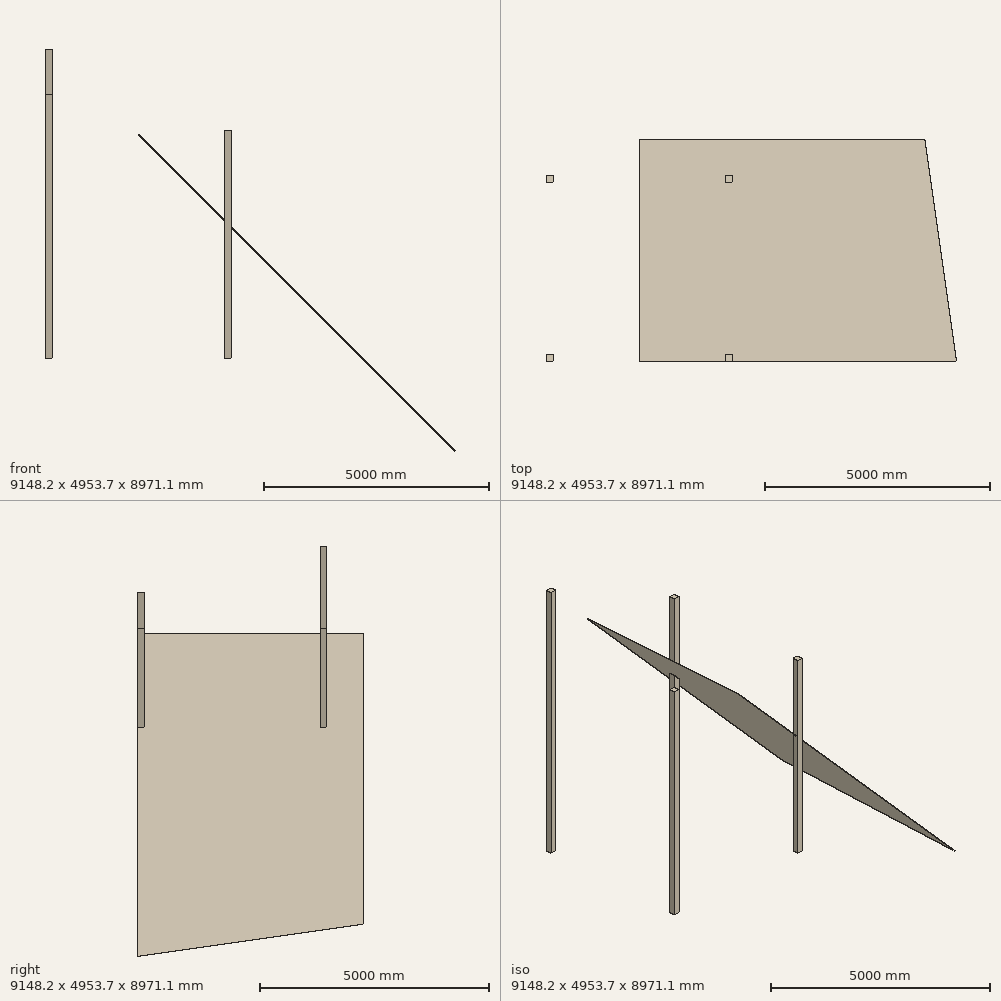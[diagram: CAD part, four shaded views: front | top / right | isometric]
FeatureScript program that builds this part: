
annotation { "Feature Type Name" : "Feature", "Feature Type Description" : "" }
export const myFeature = defineFeature(function(context is Context, id is Id, definition is map)
    precondition{}
    {
        {
            var Q0;
            Q0=qCreatedBy(makeId("Front.planeOp"),FACE);
            var sketch = newSketch(context, id + "F0", { "sketchPlane" : qUnion([Q0])});
            skLineSegment(sketch, "E0", {"start": v(3000, 7000) * mm, "end": v(3000, 6000) * mm, "construction": true});
            skLineSegment(sketch, "E1", {"start": v(3000, 6000) * mm, "end": v(3000, 3000) * mm, "construction": true});
            skLineSegment(sketch, "E2", {"start": v(3000, 3000) * mm, "end": v(0, 3000) * mm, "construction": true});
            skLineSegment(sketch, "E3", {"start": v(0, 3000) * mm, "end": v(0, 10000) * mm, "construction": true});
            skLineSegment(sketch, "E4", {"start": v(3000, 6000) * mm, "end": v(0, 6000) * mm, "construction": true});
            skLineSegment(sketch, "E5", {"start": v(0, 3000) * mm, "end": v(0, 0) * mm, "construction": true});
            skLineSegment(sketch, "E6", {"start": v(0, 0) * mm, "end": v(7000, 0) * mm, "construction": true});
            skLineSegment(sketch, "E7", {"start": v(3000, 6000) * mm, "end": v(11000, 3000) * mm, "construction": true});
            skLineSegment(sketch, "E8", {"start": v(5828, 3000) * mm, "end": v(11000, 3000) * mm, "construction": true});
            skLineSegment(sketch, "E9", {"start": v(7000, 3000) * mm, "end": v(7000, 4500) * mm, "construction": true});
            skLineSegment(sketch, "E10", {"start": v(3000, 3000) * mm, "end": v(4000, 3000) * mm, "construction": true});
            skLineSegment(sketch, "E11", {"start": v(4000, 3000) * mm, "end": v(4000, 5625) * mm, "construction": true});
            skLineSegment(sketch, "E12.0", {"start": v(3000, 7000) * mm, "end": v(0, 7000) * mm, "construction": true});
            skLineSegment(sketch, "E13", {"start": v(0, 6500) * mm, "end": v(3500, 6500) * mm, "construction": true});
            skLineSegment(sketch, "E14", {"start": v(3500, 6500) * mm, "end": v(0, 10000) * mm, "construction": true});
            skFitSpline(sketch, "E15", {"points": [v(3000, 6000) * mm, v(7000, 5200) * mm, v(9500, 3000) * mm], "startDerivative": vector(10495.04, -690.46) * mm, "endDerivative": vector(2972.96, -5651.08) * mm, "construction": true});
            skArc(sketch, "E16", {"start": v(9099.2, 3361.06) * mm, "mid": v(6978.83, 5128.79) * mm, "end": v(4291.38, 5760) * mm, "construction": true});
            skLineSegment(sketch, "E17", {"start": v(3075, 2870) * mm, "end": v(3130.8, 2870) * mm});
            skLineSegment(sketch, "E18", {"start": v(3130.8, 2870) * mm, "end": v(3181.6, 2920.8) * mm});
            skLineSegment(sketch, "E19", {"start": v(3181.6, 2920.8) * mm, "end": v(3282.6, 2920.8) * mm});
            skLineSegment(sketch, "E20", {"start": v(3282.6, 2920.8) * mm, "end": v(3333.4, 2870) * mm});
            skLineSegment(sketch, "E21", {"start": v(3232.1, 2920.8) * mm, "end": v(3232.1, 2870) * mm, "construction": true});
            skLineSegment(sketch, "E22.0", {"start": v(3075, 2990) * mm, "end": v(4015, 2990) * mm});
            skLineSegment(sketch, "E23", {"start": v(3333.4, 2870) * mm, "end": v(3389.2, 2870) * mm});
            skLineSegment(sketch, "E24.1.0.0", {"start": v(3389, 2870) * mm, "end": v(3444.8, 2870) * mm});
            skLineSegment(sketch, "E24.1.0.1", {"start": v(3444.8, 2870) * mm, "end": v(3495.6, 2920.8) * mm});
            skLineSegment(sketch, "E24.1.0.2", {"start": v(3495.6, 2920.8) * mm, "end": v(3596.6, 2920.8) * mm});
            skLineSegment(sketch, "E24.1.0.3", {"start": v(3596.6, 2920.8) * mm, "end": v(3647.4, 2870) * mm});
            skLineSegment(sketch, "E24.1.0.4", {"start": v(3647.4, 2870) * mm, "end": v(3703.2, 2870) * mm});
            skLineSegment(sketch, "E24.2.0.0", {"start": v(3703, 2870) * mm, "end": v(3758.8, 2870) * mm});
            skLineSegment(sketch, "E24.2.0.1", {"start": v(3758.8, 2870) * mm, "end": v(3809.6, 2920.8) * mm});
            skLineSegment(sketch, "E24.2.0.2", {"start": v(3809.6, 2920.8) * mm, "end": v(3910.6, 2920.8) * mm});
            skLineSegment(sketch, "E24.2.0.3", {"start": v(3910.6, 2920.8) * mm, "end": v(3961.4, 2870) * mm});
            skLineSegment(sketch, "E24.2.0.4", {"start": v(3961.4, 2870) * mm, "end": v(4017.2, 2870) * mm});
            skLineSegment(sketch, "E24.direction1", {"start": v(3075, 2870) * mm, "end": v(3389, 2870) * mm, "construction": true});
            skLineSegment(sketch, "E25", {"start": v(3075, 2990) * mm, "end": v(3075, 2870) * mm});
            skLineSegment(sketch, "E26", {"start": v(4015, 2990) * mm, "end": v(4015, 2870) * mm});
            skLineSegment(sketch, "E27.0", {"start": v(3075, 3000) * mm, "end": v(4015, 3000) * mm});
            skLineSegment(sketch, "E28.0", {"start": v(3075, 6029.43) * mm, "end": v(3075, 3000) * mm, "construction": true});
            skLineSegment(sketch, "E29", {"start": v(3000, 2990) * mm, "end": v(3000, 2720) * mm});
            skLineSegment(sketch, "E30", {"start": v(3000, 2990) * mm, "end": v(3095, 2990) * mm});
            skLineSegment(sketch, "E31", {"start": v(3095, 2990) * mm, "end": v(3095, 2979.5) * mm});
            skLineSegment(sketch, "E32", {"start": v(3095, 2979.5) * mm, "end": v(3018, 2979.5) * mm});
            skLineSegment(sketch, "E33", {"start": v(3006, 2967.5) * mm, "end": v(3006, 2742.5) * mm});
            skLineSegment(sketch, "E34", {"start": v(3018, 2730.5) * mm, "end": v(3095, 2730.5) * mm});
            skLineSegment(sketch, "E35", {"start": v(3095, 2730.5) * mm, "end": v(3095, 2720) * mm});
            skLineSegment(sketch, "E36", {"start": v(3095, 2720) * mm, "end": v(3000, 2720) * mm});
            skPoint(sketch, "E37.visualSharp", {"position": v(3006, 2979.5) * mm});
            skArc(sketch, "E37.filletArc", {"start": v(3018, 2979.5) * mm, "mid": v(3009.51, 2975.99) * mm, "end": v(3006, 2967.5) * mm});
            skPoint(sketch, "E38.visualSharp", {"position": v(3006, 2730.5) * mm});
            skArc(sketch, "E38.filletArc", {"start": v(3006, 2742.5) * mm, "mid": v(3009.51, 2734.01) * mm, "end": v(3018, 2730.5) * mm});
            skLineSegment(sketch, "E39", {"start": v(3095, 2730.5) * mm, "end": v(3095, 2870.5) * mm});
            skLineSegment(sketch, "E40", {"start": v(3095, 2730.5) * mm, "end": v(3037, 2730.5) * mm});
            skLineSegment(sketch, "E41", {"start": v(3037, 2730.5) * mm, "end": v(3037, 2738.6) * mm});
            skLineSegment(sketch, "E42", {"start": v(3037, 2738.6) * mm, "end": v(3078.9, 2738.6) * mm});
            skLineSegment(sketch, "E43", {"start": v(3090.9, 2750.6) * mm, "end": v(3090.9, 2850.4) * mm});
            skLineSegment(sketch, "E44", {"start": v(3078.9, 2862.4) * mm, "end": v(3037, 2862.4) * mm});
            skLineSegment(sketch, "E45", {"start": v(3037, 2862.4) * mm, "end": v(3037, 2870.5) * mm});
            skLineSegment(sketch, "E46", {"start": v(3037, 2870.5) * mm, "end": v(3095, 2870.5) * mm});
            skPoint(sketch, "E47.visualSharp", {"position": v(3090.9, 2738.6) * mm});
            skArc(sketch, "E47.filletArc", {"start": v(3078.9, 2738.6) * mm, "mid": v(3087.39, 2742.11) * mm, "end": v(3090.9, 2750.6) * mm});
            skPoint(sketch, "E48.visualSharp", {"position": v(3090.9, 2862.4) * mm});
            skArc(sketch, "E48.filletArc", {"start": v(3090.9, 2850.4) * mm, "mid": v(3087.39, 2858.89) * mm, "end": v(3078.9, 2862.4) * mm});
            skLineSegment(sketch, "E49", {"start": v(0, 10000) * mm, "end": v(-3500, 6500) * mm, "construction": true});
            skFitSpline(sketch, "E50.MirrorCS", {"points": [v(-3000, 6000) * mm, v(-7000, 5200) * mm, v(-9500, 3000) * mm], "startDerivative": vector(-10495.04, -690.46) * mm, "endDerivative": vector(-2972.96, -5651.08) * mm, "construction": true});
            skLineSegment(sketch, "E51", {"start": v(0, 3000) * mm, "end": v(-9500, 3000) * mm, "construction": true});
            skLineSegment(sketch, "E52", {"start": v(0, 0) * mm, "end": v(-7000, 0) * mm, "construction": true});
            skLineSegment(sketch, "E53", {"start": v(7000, 0) * mm, "end": v(7000, 3000) * mm, "construction": true});
            skLineSegment(sketch, "E54", {"start": v(3000, 0) * mm, "end": v(3000, 3000) * mm, "construction": true});
            skLineSegment(sketch, "E55.MirrorCS", {"start": v(-7000, 0) * mm, "end": v(-7000, 3000) * mm, "construction": true});
            skLineSegment(sketch, "E56.MirrorCS", {"start": v(-3000, 0) * mm, "end": v(-3000, 3000) * mm, "construction": true});
            skLineSegment(sketch, "E57.0", {"start": v(8000, -1400) * mm, "end": v(8000, 0) * mm, "construction": true});
            skLineSegment(sketch, "E58.0", {"start": v(-8000, -1400) * mm, "end": v(8000, -1400) * mm, "construction": true});
            skLineSegment(sketch, "E59", {"start": v(-8000, 0) * mm, "end": v(-8000, -1400) * mm, "construction": true});
            skSolve(sketch);
        }
        {
            var Q0;
            Q0=qCreatedBy(makeId("Top.planeOp"),FACE);
            var sketch = newSketch(context, id + "F1", { "sketchPlane" : qUnion([Q0])});
            skLineSegment(sketch, "E60.bottom", {"start": v(7000, -7000) * mm, "end": v(-7000, -7000) * mm, "construction": true});
            skLineSegment(sketch, "E60.top", {"start": v(7000, 7000) * mm, "end": v(-7000, 7000) * mm, "construction": true});
            skLineSegment(sketch, "E60.left", {"start": v(7000, -7000) * mm, "end": v(7000, 7000) * mm, "construction": true});
            skLineSegment(sketch, "E60.right", {"start": v(-7000, -7000) * mm, "end": v(-7000, 7000) * mm, "construction": true});
            skLineSegment(sketch, "E61", {"start": v(0, 0) * mm, "end": v(0, -7000) * mm, "construction": true});
            skLineSegment(sketch, "E62.bottom", {"start": v(-3000, 3000) * mm, "end": v(3000, 3000) * mm, "construction": true});
            skLineSegment(sketch, "E62.top", {"start": v(-3000, -3000) * mm, "end": v(3000, -3000) * mm, "construction": true});
            skLineSegment(sketch, "E62.left", {"start": v(-3000, 3000) * mm, "end": v(-3000, -3000) * mm, "construction": true});
            skLineSegment(sketch, "E62.right", {"start": v(3000, 3000) * mm, "end": v(3000, -3000) * mm, "construction": true});
            skLineSegment(sketch, "E63", {"start": v(0, 0) * mm, "end": v(7000, 0) * mm, "construction": true});
            skLineSegment(sketch, "E64.bottom", {"start": v(2925, -2925) * mm, "end": v(3075, -2925) * mm});
            skLineSegment(sketch, "E64.top", {"start": v(2925, -3075) * mm, "end": v(3075, -3075) * mm});
            skLineSegment(sketch, "E64.left", {"start": v(2925, -2925) * mm, "end": v(2925, -3075) * mm});
            skLineSegment(sketch, "E64.right", {"start": v(3075, -2925) * mm, "end": v(3075, -3075) * mm});
            skLineSegment(sketch, "E65.bottom", {"start": v(6925, -7075) * mm, "end": v(7075, -7075) * mm});
            skLineSegment(sketch, "E65.top", {"start": v(6925, -6925) * mm, "end": v(7075, -6925) * mm});
            skLineSegment(sketch, "E65.left", {"start": v(6925, -6925) * mm, "end": v(6925, -7075) * mm});
            skLineSegment(sketch, "E65.right", {"start": v(7075, -6925) * mm, "end": v(7075, -7075) * mm});
            skLineSegment(sketch, "E66.bottom", {"start": v(7075, -2925) * mm, "end": v(6925, -2925) * mm});
            skLineSegment(sketch, "E66.top", {"start": v(7075, -3075) * mm, "end": v(6925, -3075) * mm});
            skLineSegment(sketch, "E66.left", {"start": v(7075, -2925) * mm, "end": v(7075, -3075) * mm});
            skLineSegment(sketch, "E66.right", {"start": v(6925, -2925) * mm, "end": v(6925, -3075) * mm});
            skLineSegment(sketch, "E67.bottom", {"start": v(3075, -6925) * mm, "end": v(2925, -6925) * mm});
            skLineSegment(sketch, "E67.top", {"start": v(3075, -7075) * mm, "end": v(2925, -7075) * mm});
            skLineSegment(sketch, "E67.left", {"start": v(3075, -6925) * mm, "end": v(3075, -7075) * mm});
            skLineSegment(sketch, "E67.right", {"start": v(2925, -6925) * mm, "end": v(2925, -7075) * mm});
            skLineSegment(sketch, "E68.bottom", {"start": v(-5000, 15306.58) * mm, "end": v(5000, 15306.58) * mm, "construction": true});
            skLineSegment(sketch, "E68.top", {"start": v(-5000, 12106.58) * mm, "end": v(5000, 12106.58) * mm, "construction": true});
            skLineSegment(sketch, "E68.left", {"start": v(-5000, 15306.58) * mm, "end": v(-5000, 12106.58) * mm, "construction": true});
            skLineSegment(sketch, "E68.right", {"start": v(5000, 15306.58) * mm, "end": v(5000, 12106.58) * mm, "construction": true});
            skLineSegment(sketch, "E69.0", {"start": v(-5000, 10906.58) * mm, "end": v(5000, 10906.58) * mm, "construction": true});
            skPoint(sketch, "E70", {"position": v(0, 10906.58) * mm});
            skSolve(sketch);
        }
        {
            var Q0;
            Q0=qCreatedBy(makeId("Top.planeOp"),FACE);
            cPlane(context, id + "F2", {"entities" : qUnion([Q0]), "cplaneType" : CPlaneType.OFFSET, "offset" : 3000 * mm, "width" : 150 * mm, "height" : 150 * mm});
        }
        {
            var Q0;
            Q0=qCreatedBy(id+"F2.planeOp",FACE);
            var sketch = newSketch(context, id + "F3", { "sketchPlane" : qUnion([Q0])});
            skLineSegment(sketch, "E71", {"start": v(-3000, 3000) * mm, "end": v(-3000, -3000) * mm, "construction": true});
            skLineSegment(sketch, "E72", {"start": v(-3000, -3000) * mm, "end": v(3000, -3000) * mm, "construction": true});
            skLineSegment(sketch, "E73", {"start": v(3000, -3000) * mm, "end": v(3000, 3000) * mm, "construction": true});
            skLineSegment(sketch, "E74", {"start": v(3000, 3000) * mm, "end": v(7000, 3000) * mm, "construction": true});
            skLineSegment(sketch, "E75", {"start": v(7000, 3000) * mm, "end": v(7000, -7000) * mm, "construction": true});
            skLineSegment(sketch, "E76", {"start": v(7000, -7000) * mm, "end": v(-7000, -7000) * mm, "construction": true});
            skLineSegment(sketch, "E77", {"start": v(-7000, 3000) * mm, "end": v(-3000, 3000) * mm, "construction": true});
            skLineSegment(sketch, "E78", {"start": v(0, -2912.63) * mm, "end": v(0, -3000) * mm, "construction": true});
            skLineSegment(sketch, "E79", {"start": v(-3000, -3000) * mm, "end": v(-3000, -7000) * mm, "construction": true});
            skLineSegment(sketch, "E80", {"start": v(-4000, 3000) * mm, "end": v(-4000, -4000) * mm, "construction": true});
            skLineSegment(sketch, "E81", {"start": v(-4000, -4000) * mm, "end": v(4000, -4000) * mm, "construction": true});
            skLineSegment(sketch, "E82", {"start": v(4000, -4000) * mm, "end": v(4000, 3000) * mm, "construction": true});
            skLineSegment(sketch, "E83", {"start": v(-3000, -3000) * mm, "end": v(-9500, -9500) * mm, "construction": true});
            skLineSegment(sketch, "E84", {"start": v(-3000, 0) * mm, "end": v(-9500, 0) * mm, "construction": true});
            skLineSegment(sketch, "E85", {"start": v(0, -9500) * mm, "end": v(0, -3000) * mm, "construction": true});
            skLineSegment(sketch, "E86", {"start": v(-3000, 0) * mm, "end": v(0, 0) * mm, "construction": true});
            skLineSegment(sketch, "E87", {"start": v(0, 0) * mm, "end": v(0, -3000) * mm, "construction": true});
            skLineSegment(sketch, "E88", {"start": v(-7000, 3000) * mm, "end": v(-7000, -7000) * mm, "construction": true});
            skLineSegment(sketch, "E89.bottom", {"start": v(-9500, 9500) * mm, "end": v(9500, 9500) * mm, "construction": true});
            skLineSegment(sketch, "E89.top", {"start": v(-9500, -9500) * mm, "end": v(9500, -9500) * mm, "construction": true});
            skLineSegment(sketch, "E89.left", {"start": v(-9500, 9500) * mm, "end": v(-9500, -9500) * mm, "construction": true});
            skLineSegment(sketch, "E89.right", {"start": v(9500, 9500) * mm, "end": v(9500, -9500) * mm, "construction": true});
            skLineSegment(sketch, "E90", {"start": v(0, 0) * mm, "end": v(9500, -9500) * mm, "construction": true});
            skLineSegment(sketch, "E91.bottom", {"start": v(40.78, -3107.48) * mm, "end": v(3640.78, -3107.48) * mm, "construction": true});
            skLineSegment(sketch, "E91.top", {"start": v(40.78, -4047.48) * mm, "end": v(3640.78, -4047.48) * mm, "construction": true});
            skLineSegment(sketch, "E91.left", {"start": v(40.78, -3107.48) * mm, "end": v(40.78, -4047.48) * mm, "construction": true});
            skLineSegment(sketch, "E91.right", {"start": v(3640.78, -3107.48) * mm, "end": v(3640.78, -4047.48) * mm, "construction": true});
            skLineSegment(sketch, "E92.0.1.0", {"start": v(3640.78, -4047.48) * mm, "end": v(3640.78, -4987.48) * mm, "construction": true});
            skLineSegment(sketch, "E92.0.1.1", {"start": v(40.78, -4047.48) * mm, "end": v(40.78, -4987.48) * mm, "construction": true});
            skLineSegment(sketch, "E92.0.1.2", {"start": v(40.78, -4987.48) * mm, "end": v(3640.78, -4987.48) * mm, "construction": true});
            skLineSegment(sketch, "E92.0.2.0", {"start": v(3640.78, -4987.48) * mm, "end": v(3640.78, -5927.48) * mm, "construction": true});
            skLineSegment(sketch, "E92.0.2.1", {"start": v(40.78, -4987.48) * mm, "end": v(40.78, -5927.48) * mm, "construction": true});
            skLineSegment(sketch, "E92.0.2.2", {"start": v(40.78, -5927.48) * mm, "end": v(3640.78, -5927.48) * mm, "construction": true});
            skLineSegment(sketch, "E92.0.2.3", {"start": v(40.78, -4987.48) * mm, "end": v(3640.78, -4987.48) * mm, "construction": true});
            skLineSegment(sketch, "E92.0.3.0", {"start": v(3640.78, -5927.48) * mm, "end": v(3640.78, -6867.48) * mm, "construction": true});
            skLineSegment(sketch, "E92.0.3.1", {"start": v(40.78, -5927.48) * mm, "end": v(40.78, -6867.48) * mm, "construction": true});
            skLineSegment(sketch, "E92.0.3.2", {"start": v(40.78, -6867.48) * mm, "end": v(3640.78, -6867.48) * mm, "construction": true});
            skLineSegment(sketch, "E92.0.3.3", {"start": v(40.78, -5927.48) * mm, "end": v(3640.78, -5927.48) * mm, "construction": true});
            skLineSegment(sketch, "E92.1.0.0", {"start": v(7260.78, -3107.48) * mm, "end": v(7260.78, -4047.48) * mm, "construction": true});
            skLineSegment(sketch, "E92.1.0.1", {"start": v(3660.78, -3107.48) * mm, "end": v(3660.78, -4047.48) * mm, "construction": true});
            skLineSegment(sketch, "E92.1.0.2", {"start": v(3660.78, -4047.48) * mm, "end": v(7260.78, -4047.48) * mm, "construction": true});
            skLineSegment(sketch, "E92.1.0.3", {"start": v(3660.78, -3107.48) * mm, "end": v(7260.78, -3107.48) * mm, "construction": true});
            skLineSegment(sketch, "E92.1.1.0", {"start": v(7260.78, -4047.48) * mm, "end": v(7260.78, -4987.48) * mm, "construction": true});
            skLineSegment(sketch, "E92.1.1.1", {"start": v(3660.78, -4047.48) * mm, "end": v(3660.78, -4987.48) * mm, "construction": true});
            skLineSegment(sketch, "E92.1.1.2", {"start": v(3660.78, -4987.48) * mm, "end": v(7260.78, -4987.48) * mm, "construction": true});
            skLineSegment(sketch, "E92.1.1.3", {"start": v(3660.78, -4047.48) * mm, "end": v(7260.78, -4047.48) * mm, "construction": true});
            skLineSegment(sketch, "E92.1.2.0", {"start": v(7260.78, -4987.48) * mm, "end": v(7260.78, -5927.48) * mm, "construction": true});
            skLineSegment(sketch, "E92.1.2.1", {"start": v(3660.78, -4987.48) * mm, "end": v(3660.78, -5927.48) * mm, "construction": true});
            skLineSegment(sketch, "E92.1.2.2", {"start": v(3660.78, -5927.48) * mm, "end": v(7260.78, -5927.48) * mm, "construction": true});
            skLineSegment(sketch, "E92.1.2.3", {"start": v(3660.78, -4987.48) * mm, "end": v(7260.78, -4987.48) * mm, "construction": true});
            skLineSegment(sketch, "E92.1.3.0", {"start": v(7260.78, -5927.48) * mm, "end": v(7260.78, -6867.48) * mm, "construction": true});
            skLineSegment(sketch, "E92.1.3.1", {"start": v(3660.78, -5927.48) * mm, "end": v(3660.78, -6867.48) * mm, "construction": true});
            skLineSegment(sketch, "E92.1.3.2", {"start": v(3660.78, -6867.48) * mm, "end": v(7260.78, -6867.48) * mm, "construction": true});
            skLineSegment(sketch, "E92.1.3.3", {"start": v(3660.78, -5927.48) * mm, "end": v(7260.78, -5927.48) * mm, "construction": true});
            skLineSegment(sketch, "E92.direction1", {"start": v(3640.78, -4047.48) * mm, "end": v(7260.78, -4047.48) * mm, "construction": true});
            skLineSegment(sketch, "E92.direction2", {"start": v(3640.78, -4047.48) * mm, "end": v(3640.78, -4987.48) * mm, "construction": true});
            skLineSegment(sketch, "E93.bottom", {"start": v(3160.78, -1950.47) * mm, "end": v(7260.78, -1950.47) * mm, "construction": true});
            skLineSegment(sketch, "E93.left", {"start": v(3160.78, -1950.47) * mm, "end": v(3160.78, -2890.47) * mm, "construction": true});
            skLineSegment(sketch, "E93.right", {"start": v(7260.78, -1950.47) * mm, "end": v(7260.78, -2890.47) * mm, "construction": true});
            skLineSegment(sketch, "E94.0.1.3", {"start": v(3160.78, -2890.47) * mm, "end": v(7260.78, -2890.47) * mm, "construction": true});
            skLineSegment(sketch, "E95.0.1.0", {"start": v(3160.78, -1010.47) * mm, "end": v(7260.78, -1010.47) * mm, "construction": true});
            skLineSegment(sketch, "E95.0.1.1", {"start": v(7260.78, -1010.47) * mm, "end": v(7260.78, -1950.47) * mm, "construction": true});
            skLineSegment(sketch, "E95.0.1.3", {"start": v(3160.78, -1010.47) * mm, "end": v(3160.78, -1950.47) * mm, "construction": true});
            skLineSegment(sketch, "E95.0.2.0", {"start": v(3160.78, -70.47) * mm, "end": v(7260.78, -70.47) * mm, "construction": true});
            skLineSegment(sketch, "E95.0.2.1", {"start": v(7260.78, -70.47) * mm, "end": v(7260.78, -1010.47) * mm, "construction": true});
            skLineSegment(sketch, "E95.0.2.2", {"start": v(3160.78, -1010.47) * mm, "end": v(7260.78, -1010.47) * mm, "construction": true});
            skLineSegment(sketch, "E95.0.2.3", {"start": v(3160.78, -70.47) * mm, "end": v(3160.78, -1010.47) * mm, "construction": true});
            skLineSegment(sketch, "E95.direction1", {"start": v(3160.78, -2890.47) * mm, "end": v(3185.78, -2890.47) * mm, "construction": true});
            skLineSegment(sketch, "E95.direction2", {"start": v(3160.78, -2890.47) * mm, "end": v(3160.78, -1950.47) * mm, "construction": true});
            skLineSegment(sketch, "E96.bottom", {"start": v(-6586.29, -5052.43) * mm, "end": v(-486.29, -5052.43) * mm, "construction": true});
            skLineSegment(sketch, "E96.top", {"start": v(-6586.29, -5992.43) * mm, "end": v(-486.29, -5992.43) * mm, "construction": true});
            skLineSegment(sketch, "E96.left", {"start": v(-6586.29, -5052.43) * mm, "end": v(-6586.29, -5992.43) * mm, "construction": true});
            skLineSegment(sketch, "E96.right", {"start": v(-486.29, -5052.43) * mm, "end": v(-486.29, -5992.43) * mm, "construction": true});
            skSolve(sketch);
        }
        {
            var Q0;
            Q0=qCreatedBy(makeId("Right.planeOp"),FACE);
            var sketch = newSketch(context, id + "F4", { "sketchPlane" : qUnion([Q0])});
            skLineSegment(sketch, "E97", {"start": v(0, 10000) * mm, "end": v(-10000, 10000) * mm, "construction": true});
            skLineSegment(sketch, "E98", {"start": v(-10000, 10000) * mm, "end": v(-9000, 6500) * mm, "construction": true});
            skLineSegment(sketch, "E99", {"start": v(-9000, 7000) * mm, "end": v(-9000, 10000) * mm, "construction": true});
            skLineSegment(sketch, "E100", {"start": v(-9142.86, 7000) * mm, "end": v(0, 7000) * mm, "construction": true});
            skLineSegment(sketch, "E101", {"start": v(0, 6500) * mm, "end": v(-9000, 6500) * mm, "construction": true});
            skSolve(sketch);
        }
        {
            var Q0;
            Q0=sQuery(id+"F0.wireOp",VERTEX,"E3.end");
            var Q1;
            Q1=sQuery(id+"F0.wireOp",VERTEX,"E13.end");
            var Q2;
            Q2=sQuery(id+"F4.wireOp",VERTEX,"E97.end");
            cPlane(context, id + "F5", {"entities" : qUnion([Q0, Q1, Q2]), "cplaneType" : CPlaneType.THREE_POINT, "offset" : 25 * mm, "width" : 150 * mm, "height" : 150 * mm});
        }
        {
            var Q0;
            Q0=qCreatedBy(id+"F5.planeOp",FACE);
            var sketch = newSketch(context, id + "F6", { "sketchPlane" : qUnion([Q0])});
            skLineSegment(sketch, "E102", {"start": v(-7071.07, 0) * mm, "end": v(-7071.07, -10000) * mm});
            skLineSegment(sketch, "E103", {"start": v(-7071.07, -10000) * mm, "end": v(-2121.32, -9000) * mm});
            skLineSegment(sketch, "E104", {"start": v(-2121.32, -9000) * mm, "end": v(-2121.32, 0) * mm});
            skLineSegment(sketch, "E105", {"start": v(-2121.32, 0) * mm, "end": v(-7071.07, 0) * mm});
            skSolve(sketch);
        }
        {
            var Q0;
            Q0=makeQuery(id+"F6.imprint","IMPRINT",FACE,{"disambiguationData":[TD([[makeQuery(id+"F6.imprint","IMPRINT",EDGE,{"derivedFrom":sQuery(id+"F6.wireOp",EDGE,"E102")}),1.0]])]});
            extrude(context, id + "F7", {"entities" : qUnion([Q0]), "depth" : 3 * mm, "offsetDistance" : 25 * mm});
        }
        {
            var Q0;
            Q0=makeQuery(id+"F1.imprint","IMPRINT",FACE,{"disambiguationData":[TD([[makeQuery(id+"F1.imprint","IMPRINT",EDGE,{"derivedFrom":sQuery(id+"F1.wireOp",EDGE,"E64.bottom")}),-1.0]])]});
            extrude(context, id + "F8", {"entities" : qUnion([Q0]), "depth" : 6900 * mm, "offsetDistance" : 25 * mm});
        }
        {
            var Q0;
            Q0=makeQuery(id+"F1.imprint","IMPRINT",FACE,{"disambiguationData":[TD([[makeQuery(id+"F1.imprint","IMPRINT",EDGE,{"derivedFrom":sQuery(id+"F1.wireOp",EDGE,"E65.bottom")}),1.0]])]});
            extrude(context, id + "F9", {"entities" : qUnion([Q0]), "depth" : 5100 * mm, "offsetDistance" : 25 * mm});
        }
        {
            var Q0;
            Q0=makeQuery(id+"F1.imprint","IMPRINT",FACE,{"disambiguationData":[TD([[makeQuery(id+"F1.imprint","IMPRINT",EDGE,{"derivedFrom":sQuery(id+"F1.wireOp",EDGE,"E66.bottom")}),1.0]])]});
            extrude(context, id + "F10", {"entities" : qUnion([Q0]), "depth" : 5100 * mm, "offsetDistance" : 25 * mm});
        }
        {
            var Q0;
            Q0=makeQuery(id+"F1.imprint","IMPRINT",FACE,{"disambiguationData":[TD([[makeQuery(id+"F1.imprint","IMPRINT",EDGE,{"derivedFrom":sQuery(id+"F1.wireOp",EDGE,"E67.bottom")}),1.0]])]});
            extrude(context, id + "F11", {"entities" : qUnion([Q0]), "depth" : 5900 * mm, "offsetDistance" : 25 * mm});
        }
    });
